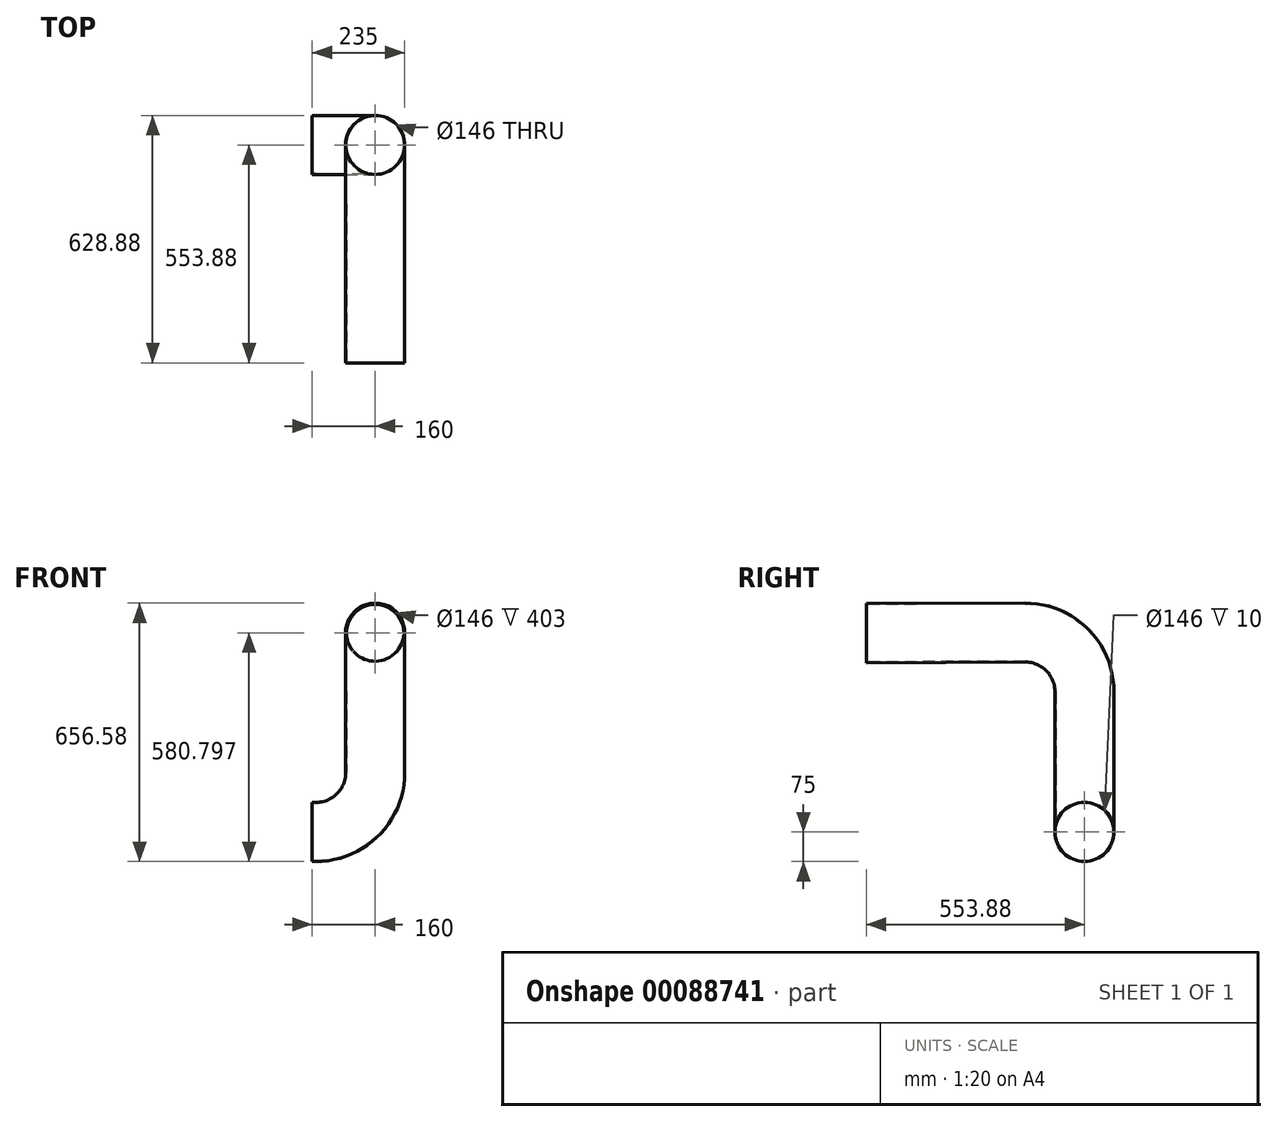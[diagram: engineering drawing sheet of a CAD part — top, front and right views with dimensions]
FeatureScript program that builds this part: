
annotation { "Feature Type Name" : "Feature", "Feature Type Description" : "" }
export const myFeature = defineFeature(function(context is Context, id is Id, definition is map)
    precondition{}
    {
        {
            var Q0;
            Q0=qCreatedBy(makeId("Front.planeOp"),FACE);
            var sketch = newSketch(context, id + "F0", { "sketchPlane" : qUnion([Q0])});
            skLineSegment(sketch, "E0", {"start": v(0, 0) * mm, "end": v(0, -175) * mm});
            skLineSegment(sketch, "E1", {"start": v(-150, -325) * mm, "end": v(-160, -325) * mm});
            skPoint(sketch, "E2.visualSharp", {"position": v(0, -325) * mm});
            skArc(sketch, "E2.filletArc", {"start": v(-150, -325) * mm, "mid": v(-43.93, -281.07) * mm, "end": v(0, -175) * mm});
            skSolve(sketch);
        }
        {
            var Q0;
            Q0=qCreatedBy(makeId("Top.planeOp"),FACE);
            var sketch = newSketch(context, id + "F1", { "sketchPlane" : qUnion([Q0])});
            skCircle(sketch, "E3", {"center": v(0, 0) * mm, "radius": 75 * mm});
            skCircle(sketch, "E4", {"center": v(0, 0) * mm, "radius": 73 * mm});
            skSolve(sketch);
        }
        {
            var Q0;
            Q0=makeQuery(id+"F1.imprint","IMPRINT",FACE,{"disambiguationData":[TD([[makeQuery(id+"F1.imprint","IMPRINT",EDGE,{"derivedFrom":sQuery(id+"F1.wireOp",EDGE,"E3")}),1.0]])]});
            var Q1;
            Q1=sQuery(id+"F0.wireOp",EDGE,"E0");
            var Q2;
            Q2=sQuery(id+"F0.wireOp",EDGE,"E2.filletArc");
            var Q3;
            Q3=sQuery(id+"F0.wireOp",EDGE,"E1");
            sweep(context, id + "F2", {"profiles" : qUnion([Q0]), "path" : qUnion([Q1, Q2, Q3])});
        }
        {
            var Q0;
            Q0=qCreatedBy(makeId("Right.planeOp"),FACE);
            var sketch = newSketch(context, id + "F3", { "sketchPlane" : qUnion([Q0])});
            skLineSegment(sketch, "E5", {"start": v(0, 0) * mm, "end": v(0, 31.58) * mm});
            skLineSegment(sketch, "E6", {"start": v(-150.6, 181.58) * mm, "end": v(-553.59, 180) * mm});
            skPoint(sketch, "E7.visualSharp", {"position": v(0, 182.18) * mm});
            skArc(sketch, "E7.filletArc", {"start": v(0, 31.58) * mm, "mid": v(-44.14, 137.86) * mm, "end": v(-150.6, 181.58) * mm});
            skSolve(sketch);
        }
        {
            var Q0;
            Q0=makeQuery(id+"F2.opSweep","CAP_FACE",FACE,{"disambiguationData":[OSD([sQuery(id+"F0.wireOp",VERTEX,"E0.start"),sQuery(id+"F1.wireOp",EDGE,"E3"),sQuery(id+"F1.wireOp",EDGE,"E4")])],"isStart":true});
            var Q1;
            Q1=sQuery(id+"F3.wireOp",EDGE,"E5");
            var Q2;
            Q2=sQuery(id+"F3.wireOp",EDGE,"E7.filletArc");
            var Q3;
            Q3=sQuery(id+"F3.wireOp",EDGE,"E6");
            sweep(context, id + "F4", {"operationType" : NewBodyOperationType.ADD, "profiles" : qUnion([Q0]), "path" : qUnion([Q1, Q2, Q3])});
        }
    });
